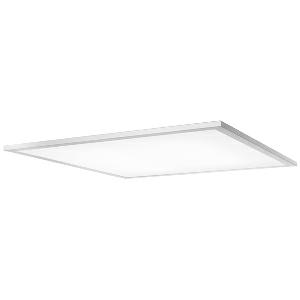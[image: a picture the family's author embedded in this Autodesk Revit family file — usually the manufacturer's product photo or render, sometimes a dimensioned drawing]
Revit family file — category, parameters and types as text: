
# Revit family: dotoo_fit_-_dfe_3000_940_d_ws_622x622mm_00815302_f420
name_source: partatom
category: Lighting Fixtures
units: mm (PartAtom-declared; Revit-internal decimal feet)

## family parameters
Cut with Voids When Loaded = No
Host = Face
Light Source = No
Part Type = Normal
Room Calculation Point = No
Round Connector Dimension = Use Diameter
Shared = No

## types (1)
- DOTOO.fit - DFE 3000/940/D/WS/622X622MM (1 x LED, 3500 lm, 4000K)
    Apparent Load = 31 VA
    Approval mark = CE
    CIE Flux Codes = 66 90 98 100 100
    Color Rendering = 90-100
    Color Temperature = 4000K
    Control Gear = Electronic ballast
    Default Elevation = 1800 mm
    Description = DFE 3000/940/D|Recessed modular luminaire|light source: LED Cold white   |work equipment: Power supply unit|luminous flux: 3500 lm|light distribution: Direct|direct ratio: approx. 100 %|color rendering index (CRI): >= 90|chromaticity tolerance:  3 SDCM|technology: Continuously dimmable|operation: External|luminaire body|material: Sectional aluminium|colour: White|weight (net): approx. 3.1 kg|mains lead: 0.80 m Connector 5 pin|design: Integrated version|glare control: Prism aperture|luminance(L65): <= 2400 cd/m|special features: DALI Load 1x, Direct light component with edge light and light-guide technology for homogenous light exit, Flicker-free, System dimension 625 x 625 mm, Strain relief with the possibility of through-wiring|
    Frequency = 60 Hz
    Height = 0 mm  [stored 0 ft]
    Lamp = 1 x LED
    Lamp Light Flux = 3500 lm
    Lamp count = 1
    Length = 622 mm
    Luminous efficacy = 113 lm/W
    Manufacturer = Waldmann
    ModVariant = No
    Model = 00815302
    Mounting Place = Ceiling
    Mounting Type = Recessed
    Number of Poles = 1
    OnlyDefault = Yes
    Power Factor = 1
    Product Name = DOTOO.fit - DFE 3000/940/D/WS/622X622MM
    Product group = Recessed luminaire
    ProductGroupID = 4
    Protection Class = Protection class II
    Protection Degree = IP 20
    RLX_Detail_Level = 1
    RLX_Emergency_Light_Flux = 0 lm
    RLX_Emergency_Type = 0
    RLX_Emergency_Type_DB = No
    RlxData = <blob elided: 26901 chars, md5=716f66ed>
    Socket = socket
    Standby Power = 0 W
    System Light Flux = 3500 lm
    System Power = 31 W
    Type Comments = Product without accessories
    Type Image = 113328000-00692486.jpg
    URL = http://relux.com
    VarID = ---
    Voltage = 230 V
    Voltage Range = 220-240 V
    Weight = 0.00 kg
    Width = 622 mm

note: [stored X ft] marks values corroborated as IEEE doubles in the binary element streams (Revit-internal decimal feet)

## geometry (parser evidence)
native form markers: Blend x4, Sweep x12
no freeform markers — native parametric forms only
